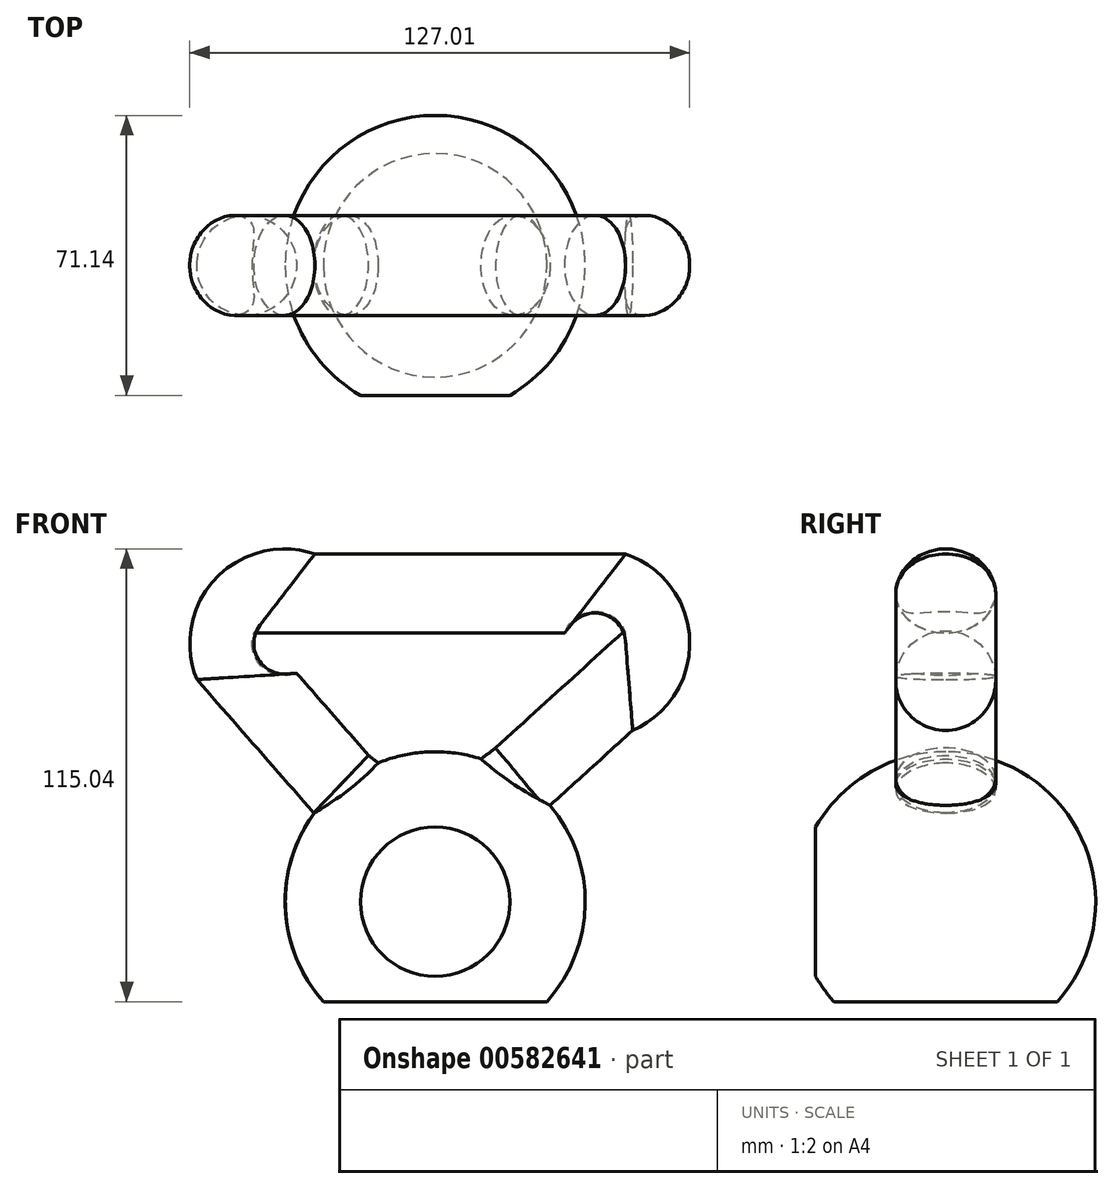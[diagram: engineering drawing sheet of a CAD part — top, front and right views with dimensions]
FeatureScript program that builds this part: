
annotation { "Feature Type Name" : "Feature", "Feature Type Description" : "" }
export const myFeature = defineFeature(function(context is Context, id is Id, definition is map)
    precondition{}
    {
        {
            var Q0;
            Q0=qCreatedBy(makeId("Front.planeOp"),FACE);
            var sketch = newSketch(context, id + "F0", { "sketchPlane" : qUnion([Q0])});
            skCircle(sketch, "E0", {"center": v(0, 0) * mm, "radius": 38.1 * mm});
            skLineSegment(sketch, "E1", {"start": v(0, 0) * mm, "end": v(0, 38.1) * mm});
            skLineSegment(sketch, "E2", {"start": v(0, 38.1) * mm, "end": v(0, -38.1) * mm});
            skSolve(sketch);
        }
        {
            var Q0;
            {var subQ0=sQuery(id+"F0.wireOp",EDGE,"E2");var subQ4=makeQuery(id+"F0.imprint","IMPRINT",VERTEX,{"derivedFrom":subQ0});Q0=makeQuery(id+"F0.imprint","IMPRINT",FACE,{"disambiguationData":[TD([[makeQuery(id+"F0.imprint","IMPRINT",EDGE,{"disambiguationData":[TD([[subQ4,1.0]])],"derivedFrom":subQ0}),1.0]])]});}
            var Q1;
            Q1=sQuery(id+"F0.wireOp",EDGE,"E2");
            revolve(context, id + "F1", {"entities" : qUnion([Q0]), "axis" : qUnion([Q1]), "revolveType" : RevolveType.FULL});
        }
        {
            var Q0;
            Q0=qCreatedBy(makeId("Front.planeOp"),FACE);
            var sketch = newSketch(context, id + "F2", { "sketchPlane" : qUnion([Q0])});
            skLineSegment(sketch, "E3.bottom", {"start": v(0, -25.4) * mm, "end": v(49.03, -25.4) * mm});
            skLineSegment(sketch, "E3.top", {"start": v(0, -47.38) * mm, "end": v(49.03, -47.38) * mm});
            skLineSegment(sketch, "E3.left", {"start": v(0, -25.4) * mm, "end": v(0, -47.38) * mm});
            skLineSegment(sketch, "E3.right", {"start": v(49.03, -25.4) * mm, "end": v(49.03, -47.38) * mm});
            skLineSegment(sketch, "E4.bottom", {"start": v(0, -25.4) * mm, "end": v(-38.4, -25.4) * mm});
            skLineSegment(sketch, "E4.top", {"start": v(0, -49.37) * mm, "end": v(-38.4, -49.37) * mm});
            skLineSegment(sketch, "E4.left", {"start": v(0, -25.4) * mm, "end": v(0, -49.37) * mm});
            skLineSegment(sketch, "E4.right", {"start": v(-38.4, -25.4) * mm, "end": v(-38.4, -49.37) * mm});
            skSolve(sketch);
        }
        {
            var Q0;
            {var subQ3=sQuery(id+"F2.wireOp",EDGE,"E4.bottom");Q0=makeQuery(id+"F2.imprint","IMPRINT",FACE,{"disambiguationData":[TD([[makeQuery(id+"F2.imprint","IMPRINT",EDGE,{"derivedFrom":subQ3}),1.0]])]});}
            var Q1;
            {var subQ0=sQuery(id+"F2.wireOp",EDGE,"E3.bottom");Q1=makeQuery(id+"F2.imprint","IMPRINT",FACE,{"disambiguationData":[TD([[makeQuery(id+"F2.imprint","IMPRINT",EDGE,{"derivedFrom":subQ0}),-1.0]])]});}
            extrude(context, id + "F3", {"entities" : qUnion([Q0, Q1]), "operationType" : NewBodyOperationType.REMOVE, "endBound" : BoundingType.SYMMETRIC, "oppositeDirection" : true, "depth" : 254 * mm, "offsetDistance" : 25.4 * mm});
        }
        {
            var Q0;
            Q0=qCreatedBy(makeId("Front.planeOp"),FACE);
            var sketch = newSketch(context, id + "F4", { "sketchPlane" : qUnion([Q0])});
            skLineSegment(sketch, "E5", {"start": v(21.79, 31.35) * mm, "end": v(49.16, 56.2) * mm});
            skLineSegment(sketch, "E6", {"start": v(40.62, 78.3) * mm, "end": v(-38.31, 78.3) * mm});
            skLineSegment(sketch, "E7", {"start": v(-47.86, 57.23) * mm, "end": v(-23.89, 29.87) * mm});
            skPoint(sketch, "E8.visualSharp", {"position": v(73.5, 78.3) * mm});
            skArc(sketch, "E8.filletArc", {"start": v(49.16, 56.2) * mm, "mid": v(52.47, 70.18) * mm, "end": v(40.62, 78.3) * mm});
            skPoint(sketch, "E9.visualSharp", {"position": v(-66.33, 78.3) * mm});
            skArc(sketch, "E9.filletArc", {"start": v(-38.31, 78.3) * mm, "mid": v(-49.88, 70.84) * mm, "end": v(-47.86, 57.23) * mm});
            skSolve(sketch);
        }
        {
            var Q0;
            Q0=qCreatedBy(makeId("Right.planeOp"),FACE);
            var sketch = newSketch(context, id + "F5", { "sketchPlane" : qUnion([Q0])});
            skCircle(sketch, "E10", {"center": v(0, 14.55) * mm, "radius": 12.7 * mm});
            skSolve(sketch);
        }
        {
            var Q0;
            Q0=qCreatedBy(makeId("Front.planeOp"),FACE);
            var sketch = newSketch(context, id + "F6", { "sketchPlane" : qUnion([Q0])});
            skLineSegment(sketch, "E11", {"start": v(0, 14.55) * mm, "end": v(21.79, 31.35) * mm});
            skSolve(sketch);
        }
        {
            var Q0;
            Q0=qCreatedBy(makeId("Front.planeOp"),FACE);
            var sketch = newSketch(context, id + "F7", { "sketchPlane" : qUnion([Q0])});
            skLineSegment(sketch, "E12", {"start": v(-23.88, 29.87) * mm, "end": v(-11.87, 20.27) * mm});
            skSolve(sketch);
        }
        {
            var Q0;
            Q0 = qSketchRegion(id + "F5", true);
            var Q1;
            Q1 = qConstructionFilter(qBodyType(qCreatedBy(id + "F4" ,EDGE), BodyType.WIRE), ConstructionObject.NO);
            var Q2;
            Q2 = qConstructionFilter(qBodyType(qCreatedBy(id + "F6" ,EDGE), BodyType.WIRE), ConstructionObject.NO);
            var Q3;
            Q3 = qConstructionFilter(qBodyType(qCreatedBy(id + "F7" ,EDGE), BodyType.WIRE), ConstructionObject.NO);
            sweep(context, id + "F8", {"operationType" : NewBodyOperationType.ADD, "profiles" : qUnion([Q0]), "path" : qUnion([Q1, Q2, Q3])});
        }
        {
            var Q0;
            Q0=qCreatedBy(makeId("Right.planeOp"),FACE);
            var sketch = newSketch(context, id + "F9", { "sketchPlane" : qUnion([Q0])});
            skLineSegment(sketch, "E13.bottom", {"start": v(-33.04, 50.55) * mm, "end": v(-53.87, 50.55) * mm});
            skLineSegment(sketch, "E13.top", {"start": v(-33.04, -46.03) * mm, "end": v(-53.87, -46.03) * mm});
            skLineSegment(sketch, "E13.left", {"start": v(-33.04, 50.55) * mm, "end": v(-33.04, -46.03) * mm});
            skLineSegment(sketch, "E13.right", {"start": v(-53.87, 50.55) * mm, "end": v(-53.87, -46.03) * mm});
            skSolve(sketch);
        }
        {
            var Q0;
            Q0=makeQuery(id+"F9.imprint","IMPRINT",FACE,{"disambiguationData":[TD([[makeQuery(id+"F9.imprint","IMPRINT",EDGE,{"derivedFrom":sQuery(id+"F9.wireOp",EDGE,"E13.bottom")}),1.0]])]});
            extrude(context, id + "F10", {"entities" : qUnion([Q0]), "operationType" : NewBodyOperationType.REMOVE, "endBound" : BoundingType.SYMMETRIC, "oppositeDirection" : true, "depth" : 254 * mm, "offsetDistance" : 25.4 * mm});
        }
    });
